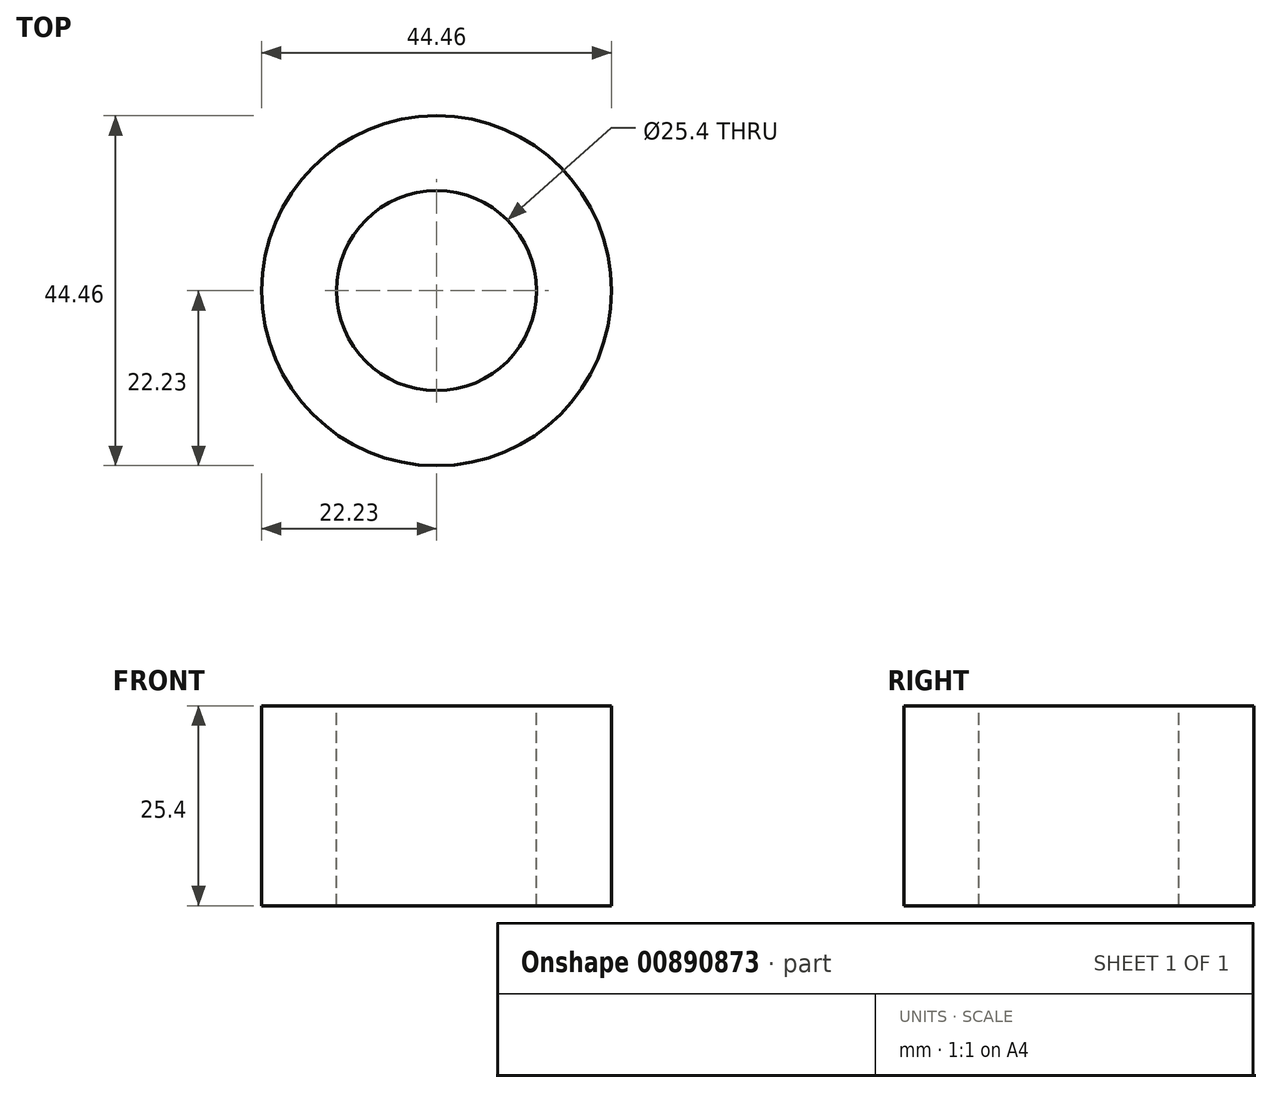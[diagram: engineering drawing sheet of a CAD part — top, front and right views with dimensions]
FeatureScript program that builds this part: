
annotation { "Feature Type Name" : "Feature", "Feature Type Description" : "" }
export const myFeature = defineFeature(function(context is Context, id is Id, definition is map)
    precondition{}
    {
        {
            var Q0;
            Q0=qCreatedBy(makeId("Top.planeOp"),FACE);
            var sketch = newSketch(context, id + "F0", { "sketchPlane" : qUnion([Q0])});
            skCircle(sketch, "E0", {"center": v(0, 0) * mm, "radius": 22.23 * mm});
            skSolve(sketch);
        }
        {
            var Q0;
            Q0 = qSketchRegion(id + "F0", true);
            var Q1;
            Q1=makeQuery(id+"F0.imprint","IMPRINT",FACE,{"disambiguationData":[TD([[makeQuery(id+"F0.imprint","IMPRINT",EDGE,{"derivedFrom":sQuery(id+"F0.wireOp",EDGE,"E0")}),1.0]])]});
            extrude(context, id + "F1", {"entities" : qUnion([Q0, Q1]), "depth" : 25.4 * mm, "offsetDistance" : 25.4 * mm});
        }
        {
            var Q0;
            Q0=makeQuery(id+"F1.opExtrude","CAP_FACE",FACE,{"disambiguationData":[OSD([sQuery(id+"F0.wireOp",EDGE,"E0")])],"isStart":false});
            var sketch = newSketch(context, id + "F2", { "sketchPlane" : qUnion([Q0])});
            skCircle(sketch, "E1", {"center": v(0, 0) * mm, "radius": 12.7 * mm});
            skSolve(sketch);
        }
        {
            var Q0;
            Q0 = qSketchRegion(id + "F2", true);
            extrude(context, id + "F3", {"entities" : qUnion([Q0]), "operationType" : NewBodyOperationType.REMOVE, "oppositeDirection" : true, "depth" : 25.4 * mm, "offsetDistance" : 25.4 * mm});
        }
    });
